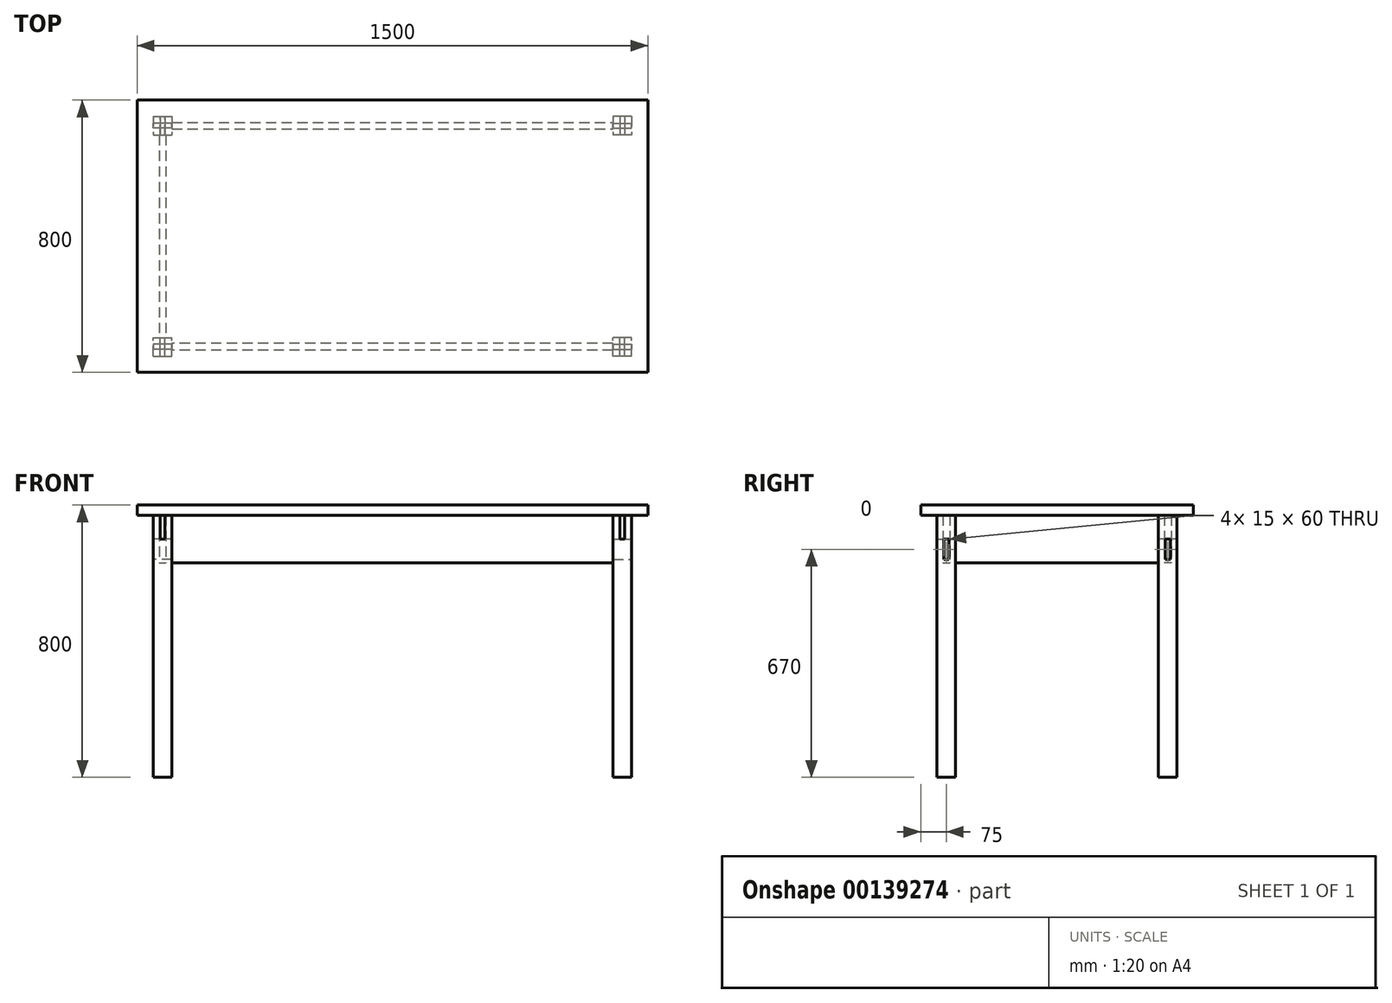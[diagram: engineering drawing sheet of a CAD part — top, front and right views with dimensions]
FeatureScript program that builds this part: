
annotation { "Feature Type Name" : "Feature", "Feature Type Description" : "" }
export const myFeature = defineFeature(function(context is Context, id is Id, definition is map)
    precondition{}
    {
        {
            assignVariable(context, id + "F0", {"name" : "oh", "anyValue" : 75});
        }
        {
            var Q0;
            Q0=qCreatedBy(makeId("Front.planeOp"),FACE);
            var sketch = newSketch(context, id + "F1", { "sketchPlane" : qUnion([Q0])});
            skLineSegment(sketch, "E0.bottom", {"start": v(-750, 800) * mm, "end": v(750, 800) * mm, "construction": true});
            skLineSegment(sketch, "E0.top", {"start": v(-750, 0) * mm, "end": v(750, 0) * mm, "construction": true});
            skLineSegment(sketch, "E0.left", {"start": v(-750, 800) * mm, "end": v(-750, 0) * mm, "construction": true});
            skLineSegment(sketch, "E0.right", {"start": v(750, 800) * mm, "end": v(750, 0) * mm, "construction": true});
            skLineSegment(sketch, "E1", {"start": v(0, 0) * mm, "end": v(0, 800) * mm, "construction": true});
            skLineSegment(sketch, "E2.bottom", {"start": v(-750, 800) * mm, "end": v(750, 800) * mm});
            skLineSegment(sketch, "E2.top", {"start": v(-750, 770) * mm, "end": v(750, 770) * mm});
            skLineSegment(sketch, "E2.left", {"start": v(-750, 800) * mm, "end": v(-750, 770) * mm});
            skLineSegment(sketch, "E2.right", {"start": v(750, 800) * mm, "end": v(750, 770) * mm});
            skLineSegment(sketch, "E3.bottom", {"start": v(-702.5, 770) * mm, "end": v(-647.5, 770) * mm});
            skLineSegment(sketch, "E3.top", {"start": v(-702.5, 0) * mm, "end": v(-647.5, 0) * mm});
            skLineSegment(sketch, "E3.left", {"start": v(-702.5, 770) * mm, "end": v(-702.5, 0) * mm});
            skLineSegment(sketch, "E3.right", {"start": v(-647.5, 770) * mm, "end": v(-647.5, 0) * mm});
            skLineSegment(sketch, "E4.bottom", {"start": v(-647.5, 770) * mm, "end": v(647.5, 770) * mm});
            skLineSegment(sketch, "E4.top", {"start": v(-647.5, 630) * mm, "end": v(647.5, 630) * mm});
            skLineSegment(sketch, "E4.left", {"start": v(-647.5, 770) * mm, "end": v(-647.5, 630) * mm});
            skLineSegment(sketch, "E4.right", {"start": v(647.5, 770) * mm, "end": v(647.5, 630) * mm});
            skLineSegment(sketch, "E5.bottom", {"start": v(-647.5, 700) * mm, "end": v(-702.5, 700) * mm});
            skLineSegment(sketch, "E5.top", {"start": v(-647.5, 640) * mm, "end": v(-702.5, 640) * mm});
            skLineSegment(sketch, "E5.left", {"start": v(-647.5, 700) * mm, "end": v(-647.5, 640) * mm});
            skLineSegment(sketch, "E5.right", {"start": v(-702.5, 700) * mm, "end": v(-702.5, 640) * mm});
            skLineSegment(sketch, "E6", {"start": v(-675, 770) * mm, "end": v(-675, 0) * mm, "construction": true});
            skLineSegment(sketch, "E7.MirrorCS", {"start": v(647.5, 640) * mm, "end": v(702.5, 640) * mm});
            skLineSegment(sketch, "E8.MirrorCS", {"start": v(702.5, 700) * mm, "end": v(702.5, 640) * mm});
            skLineSegment(sketch, "E9.MirrorCS", {"start": v(647.5, 700) * mm, "end": v(702.5, 700) * mm});
            skLineSegment(sketch, "E10.MirrorCS", {"start": v(647.5, 700) * mm, "end": v(647.5, 640) * mm});
            skSolve(sketch);
        }
        {
            var Q0;
            Q0=makeQuery(id+"F1.imprint","IMPRINT",FACE,{"disambiguationData":[TD([[makeQuery(id+"F1.imprint","IMPRINT",EDGE,{"derivedFrom":sQuery(id+"F1.wireOp",EDGE,"E2.bottom")}),-1.0]])]});
            extrude(context, id + "F2", {"entities" : qUnion([Q0]), "endBound" : BoundingType.SYMMETRIC, "depth" : 800 * mm});
        }
        {
            var Q0;
            Q0=makeQuery(id+"F2.opExtrude","CAP_FACE",FACE,{"disambiguationData":[OSD([sQuery(id+"F1.wireOp",EDGE,"E2.bottom"),sQuery(id+"F1.wireOp",EDGE,"E2.top"),sQuery(id+"F1.wireOp",EDGE,"E2.left"),sQuery(id+"F1.wireOp",EDGE,"E2.right"),sQuery(id+"F1.wireOp",EDGE,"E3.bottom"),sQuery(id+"F1.wireOp",EDGE,"E4.bottom")])],"isStart":false});
            cPlane(context, id + "F3", {"entities" : qUnion([Q0]), "cplaneType" : CPlaneType.OFFSET, "offset" : (getVariable(context, 'oh')) * mm, "oppositeDirection" : true, "width" : 150 * mm, "height" : 150 * mm});
        }
        {
            var Q0;
            Q0=qCreatedBy(id+"F3.planeOp",FACE);
            var sketch = newSketch(context, id + "F4", { "sketchPlane" : qUnion([Q0])});
            skLineSegment(sketch, "E11.0.0", {"start": v(647.5, 770) * mm, "end": v(-647.5, 770) * mm});
            skLineSegment(sketch, "E11.0.1", {"start": v(-647.5, 770) * mm, "end": v(-647.5, 700) * mm});
            skLineSegment(sketch, "E11.0.2", {"start": v(-647.5, 700) * mm, "end": v(-647.5, 640) * mm});
            skLineSegment(sketch, "E11.0.3", {"start": v(-647.5, 640) * mm, "end": v(-647.5, 630) * mm});
            skLineSegment(sketch, "E11.0.4", {"start": v(-647.5, 630) * mm, "end": v(647.5, 630) * mm});
            skLineSegment(sketch, "E11.0.5", {"start": v(647.5, 630) * mm, "end": v(647.5, 640) * mm});
            skLineSegment(sketch, "E11.0.6", {"start": v(647.5, 640) * mm, "end": v(647.5, 700) * mm});
            skLineSegment(sketch, "E11.0.7", {"start": v(647.5, 700) * mm, "end": v(647.5, 770) * mm});
            skLineSegment(sketch, "E11.1", {"start": v(702.5, 700) * mm, "end": v(702.5, 640) * mm});
            skLineSegment(sketch, "E11.2.0", {"start": v(647.5, 700) * mm, "end": v(647.5, 640) * mm});
            skLineSegment(sketch, "E11.2.1", {"start": v(647.5, 640) * mm, "end": v(702.5, 640) * mm});
            skLineSegment(sketch, "E11.2.2", {"start": v(702.5, 640) * mm, "end": v(702.5, 700) * mm});
            skLineSegment(sketch, "E11.2.3", {"start": v(702.5, 700) * mm, "end": v(647.5, 700) * mm});
            skLineSegment(sketch, "E12.0", {"start": v(-647.5, 700) * mm, "end": v(-702.5, 700) * mm});
            skLineSegment(sketch, "E12.1", {"start": v(-647.5, 640) * mm, "end": v(-702.5, 640) * mm});
            skLineSegment(sketch, "E12.2", {"start": v(-702.5, 700) * mm, "end": v(-702.5, 640) * mm});
            skSolve(sketch);
        }
        {
            var Q0;
            Q0=makeQuery(id+"F2.opExtrude","SWEPT_FACE",FACE,{"disambiguationData":[OSD([sQuery(id+"F1.wireOp",EDGE,"E2.left")])]});
            cPlane(context, id + "F5", {"entities" : qUnion([Q0]), "cplaneType" : CPlaneType.OFFSET, "offset" : (getVariable(context, 'oh')) * mm, "oppositeDirection" : true, "width" : 150 * mm, "height" : 150 * mm});
        }
        {
            var Q0;
            Q0=qCreatedBy(id+"F5.planeOp",FACE);
            var sketch = newSketch(context, id + "F6", { "sketchPlane" : qUnion([Q0])});
            skLineSegment(sketch, "E13.0", {"start": v(325, 700) * mm, "end": v(325, 640) * mm, "construction": true});
            skLineSegment(sketch, "E14.bottom", {"start": v(317.5, 700) * mm, "end": v(332.5, 700) * mm});
            skLineSegment(sketch, "E14.top", {"start": v(317.5, 640) * mm, "end": v(332.5, 640) * mm});
            skLineSegment(sketch, "E14.left", {"start": v(317.5, 700) * mm, "end": v(317.5, 640) * mm});
            skLineSegment(sketch, "E14.right", {"start": v(332.5, 700) * mm, "end": v(332.5, 640) * mm});
            skLineSegment(sketch, "E15.0", {"start": v(0, 770) * mm, "end": v(0, 0) * mm, "construction": true});
            skLineSegment(sketch, "E16.0", {"start": v(400, 770) * mm, "end": v(-400, 770) * mm, "construction": true});
            skLineSegment(sketch, "E17", {"start": v(325, 640) * mm, "end": v(325, 0) * mm, "construction": true});
            skLineSegment(sketch, "E18", {"start": v(325, 700) * mm, "end": v(325, 770) * mm, "construction": true});
            skLineSegment(sketch, "E19.bottom", {"start": v(-297.5, 770) * mm, "end": v(297.5, 770) * mm});
            skLineSegment(sketch, "E19.top", {"start": v(-297.5, 630) * mm, "end": v(297.5, 630) * mm});
            skLineSegment(sketch, "E19.left", {"start": v(-297.5, 770) * mm, "end": v(-297.5, 630) * mm});
            skLineSegment(sketch, "E19.right", {"start": v(297.5, 770) * mm, "end": v(297.5, 630) * mm});
            skLineSegment(sketch, "E20.bottom", {"start": v(297.5, 700) * mm, "end": v(352.5, 700) * mm});
            skLineSegment(sketch, "E20.top", {"start": v(297.5, 770) * mm, "end": v(352.5, 770) * mm});
            skLineSegment(sketch, "E20.left", {"start": v(297.5, 700) * mm, "end": v(297.5, 770) * mm});
            skLineSegment(sketch, "E20.right", {"start": v(352.5, 700) * mm, "end": v(352.5, 770) * mm});
            skLineSegment(sketch, "E21.bottom", {"start": v(335.91, 770) * mm, "end": v(335.7, 770) * mm});
            skLineSegment(sketch, "E21.top", {"start": v(335.91, 770) * mm, "end": v(335.7, 770) * mm});
            skLineSegment(sketch, "E21.left", {"start": v(335.91, 770) * mm, "end": v(335.91, 770) * mm});
            skLineSegment(sketch, "E21.right", {"start": v(335.7, 770) * mm, "end": v(335.7, 770) * mm});
            skLineSegment(sketch, "E22.MirrorCS", {"start": v(-352.5, 700) * mm, "end": v(-352.5, 770) * mm});
            skLineSegment(sketch, "E23.MirrorCS", {"start": v(-335.91, 770) * mm, "end": v(-335.7, 770) * mm});
            skLineSegment(sketch, "E24.MirrorCS", {"start": v(-317.5, 700) * mm, "end": v(-332.5, 700) * mm});
            skLineSegment(sketch, "E25.MirrorCS", {"start": v(-297.5, 700) * mm, "end": v(-352.5, 700) * mm});
            skLineSegment(sketch, "E26.MirrorCS", {"start": v(-297.5, 770) * mm, "end": v(-352.5, 770) * mm});
            skLineSegment(sketch, "E27.MirrorCS", {"start": v(-335.7, 770) * mm, "end": v(-335.7, 770) * mm});
            skLineSegment(sketch, "E28.MirrorCS", {"start": v(-297.5, 700) * mm, "end": v(-297.5, 770) * mm});
            skLineSegment(sketch, "E29.MirrorCS", {"start": v(-335.91, 770) * mm, "end": v(-335.91, 770) * mm});
            skLineSegment(sketch, "E30.MirrorCS", {"start": v(-325, 700) * mm, "end": v(-325, 770) * mm, "construction": true});
            skSolve(sketch);
        }
        {
            var Q0;
            Q0=makeQuery(id+"F4.imprint","IMPRINT",FACE,{"disambiguationData":[TD([[makeQuery(id+"F4.imprint","IMPRINT",EDGE,{"derivedFrom":sQuery(id+"F4.wireOp",EDGE,"E11.0.0")}),1.0]])]});
            var sketch = newSketch(context, id + "F7", { "sketchPlane" : qUnion([Q0])});
            skLineSegment(sketch, "E31.0", {"start": v(-675, 700) * mm, "end": v(-675, 770) * mm, "construction": true});
            skLineSegment(sketch, "E32.bottom", {"start": v(-682.5, 770) * mm, "end": v(-667.5, 770) * mm});
            skLineSegment(sketch, "E32.top", {"start": v(-682.5, 700) * mm, "end": v(-667.5, 700) * mm});
            skLineSegment(sketch, "E32.left", {"start": v(-682.5, 770) * mm, "end": v(-682.5, 700) * mm});
            skLineSegment(sketch, "E32.right", {"start": v(-667.5, 770) * mm, "end": v(-667.5, 700) * mm});
            skSolve(sketch);
        }
        {
            var Q0;
            Q0=makeQuery(id+"F4.imprint","IMPRINT",FACE,{"disambiguationData":[TD([[makeQuery(id+"F4.imprint","IMPRINT",EDGE,{"derivedFrom":sQuery(id+"F4.wireOp",EDGE,"E11.0.0")}),1.0]])]});
            var sketch = newSketch(context, id + "F8", { "sketchPlane" : qUnion([Q0])});
            skLineSegment(sketch, "E33.0", {"start": v(-702.5, 770) * mm, "end": v(-702.5, 0) * mm});
            skLineSegment(sketch, "E33.1", {"start": v(-647.5, 770) * mm, "end": v(-647.5, 0) * mm});
            skLineSegment(sketch, "E33.2", {"start": v(-702.5, 0) * mm, "end": v(-647.5, 0) * mm});
            skLineSegment(sketch, "E34", {"start": v(-702.5, 770) * mm, "end": v(-682.5, 770) * mm});
            skLineSegment(sketch, "E35.0", {"start": v(-682.5, 770) * mm, "end": v(-682.5, 700) * mm});
            skLineSegment(sketch, "E35.1", {"start": v(-667.5, 770) * mm, "end": v(-667.5, 700) * mm});
            skLineSegment(sketch, "E35.2", {"start": v(-682.5, 700) * mm, "end": v(-667.5, 700) * mm});
            skLineSegment(sketch, "E36.trimOffspring", {"start": v(-667.5, 770) * mm, "end": v(-647.5, 770) * mm});
            skSolve(sketch);
        }
        {
            var Q0;
            Q0=makeQuery(id+"F6.imprint","IMPRINT",FACE,{"disambiguationData":[TD([[makeQuery(id+"F6.imprint","IMPRINT",EDGE,{"derivedFrom":sQuery(id+"F6.wireOp",EDGE,"E19.bottom")}),-1.0]])]});
            var sketch = newSketch(context, id + "F9", { "sketchPlane" : qUnion([Q0])});
            skLineSegment(sketch, "E37.0", {"start": v(317.5, 640) * mm, "end": v(332.5, 640) * mm});
            skLineSegment(sketch, "E37.1", {"start": v(317.5, 700) * mm, "end": v(317.5, 640) * mm});
            skLineSegment(sketch, "E37.2", {"start": v(332.5, 700) * mm, "end": v(332.5, 640) * mm});
            skLineSegment(sketch, "E37.3", {"start": v(317.5, 700) * mm, "end": v(332.5, 700) * mm});
            skSolve(sketch);
        }
        {
            var Q0;
            Q0=makeQuery(id+"F4.imprint","IMPRINT",FACE,{"disambiguationData":[TD([[makeQuery(id+"F4.imprint","IMPRINT",EDGE,{"derivedFrom":sQuery(id+"F4.wireOp",EDGE,"E11.0.0")}),1.0]])]});
            extrude(context, id + "F10", {"entities" : qUnion([Q0]), "endBound" : BoundingType.SYMMETRIC, "depth" : 20 * mm});
        }
        {
            var Q0;
            Q0=makeQuery(id+"F4.imprint","IMPRINT",FACE,{"disambiguationData":[TD([[makeQuery(id+"F4.imprint","IMPRINT",EDGE,{"derivedFrom":sQuery(id+"F4.wireOp",EDGE,"E11.0.2")}),-1.0]])]});
            var Q1;
            Q1=makeQuery(id+"F4.imprint","IMPRINT",FACE,{"disambiguationData":[TD([[makeQuery(id+"F4.imprint","IMPRINT",EDGE,{"derivedFrom":sQuery(id+"F4.wireOp",EDGE,"E11.2.0")}),1.0]])]});
            extrude(context, id + "F11", {"entities" : qUnion([Q0, Q1]), "operationType" : NewBodyOperationType.ADD, "endBound" : BoundingType.SYMMETRIC, "depth" : 15 * mm});
        }
        {
            var Q0;
            Q0=makeQuery(id+"F9.imprint","IMPRINT",FACE,{"disambiguationData":[TD([[makeQuery(id+"F9.imprint","IMPRINT",EDGE,{"derivedFrom":makeQuery(id+"F6.imprint","IMPRINT",EDGE,{"derivedFrom":sQuery(id+"F6.wireOp",EDGE,"E19.bottom")})}),-1.0]])]});
            extrude(context, id + "F12", {"entities" : qUnion([Q0]), "endBound" : BoundingType.SYMMETRIC, "depth" : 20 * mm});
        }
        {
            var Q0;
            {var subQ0=sQuery(id+"F6.wireOp",EDGE,"E22.MirrorCS");Q0=makeQuery(id+"F6.imprint","IMPRINT",FACE,{"disambiguationData":[TD([[makeQuery(id+"F6.imprint","IMPRINT",EDGE,{"derivedFrom":subQ0}),-1.0]])]});}
            var Q1;
            {var subQ3=sQuery(id+"F6.wireOp",EDGE,"E20.left");Q1=makeQuery(id+"F6.imprint","IMPRINT",FACE,{"disambiguationData":[TD([[makeQuery(id+"F6.imprint","IMPRINT",EDGE,{"derivedFrom":subQ3}),-1.0]])]});}
            extrude(context, id + "F13", {"entities" : qUnion([Q0, Q1]), "operationType" : NewBodyOperationType.ADD, "endBound" : BoundingType.SYMMETRIC, "depth" : 15 * mm});
        }
        {
            var Q0;
            Q0=makeQuery(id+"F8.imprint","IMPRINT",FACE,{"disambiguationData":[TD([[makeQuery(id+"F8.imprint","IMPRINT",EDGE,{"derivedFrom":sQuery(id+"F8.wireOp",EDGE,"E33.0")}),1.0]])]});
            extrude(context, id + "F14", {"entities" : qUnion([Q0]), "endBound" : BoundingType.SYMMETRIC, "depth" : 55 * mm});
        }
        {
            var Q0;
            Q0=makeQuery(id+"F9.imprint","IMPRINT",FACE,{"disambiguationData":[TD([[makeQuery(id+"F9.imprint","IMPRINT",EDGE,{"derivedFrom":sQuery(id+"F9.wireOp",EDGE,"E37.0")}),1.0]])]});
            extrude(context, id + "F15", {"entities" : qUnion([Q0]), "operationType" : NewBodyOperationType.REMOVE, "endBound" : BoundingType.SYMMETRIC, "oppositeDirection" : true, "depth" : 55 * mm});
        }
        {
            var Q0;
            Q0=makeQuery(id+"F10.opExtrude","SWEPT_BODY",BODY,{"disambiguationData":[OSD([sQuery(id+"F4.wireOp",EDGE,"E11.0.0"),sQuery(id+"F4.wireOp",EDGE,"E11.0.1"),sQuery(id+"F4.wireOp",EDGE,"E11.0.2"),sQuery(id+"F4.wireOp",EDGE,"E11.0.3"),sQuery(id+"F4.wireOp",EDGE,"E11.0.4"),sQuery(id+"F4.wireOp",EDGE,"E11.0.5"),sQuery(id+"F4.wireOp",EDGE,"E11.0.7"),sQuery(id+"F4.wireOp",EDGE,"E11.2.0")])]});
            var Q1;
            Q1=makeQuery(id+"F14.opExtrude","SWEPT_BODY",BODY,{"disambiguationData":[OSD([sQuery(id+"F8.wireOp",EDGE,"E33.0"),sQuery(id+"F8.wireOp",EDGE,"E33.1"),sQuery(id+"F8.wireOp",EDGE,"E33.2"),sQuery(id+"F8.wireOp",EDGE,"E34"),sQuery(id+"F8.wireOp",EDGE,"E35.0"),sQuery(id+"F8.wireOp",EDGE,"E35.1"),sQuery(id+"F8.wireOp",EDGE,"E35.2"),sQuery(id+"F8.wireOp",EDGE,"E36.trimOffspring")])]});
            var Q2;
            Q2=sQuery(id+"F1.wireOp",EDGE,"E1");
            circularPattern(context, id + "F16", {"entities" : qUnion([Q0, Q1]), "axis" : qUnion([Q2]), "angle" : 180 * degree, "instanceCount" : 2});
        }
        {
            var Q0;
            Q0=makeQuery(id+"F14.opExtrude","SWEPT_BODY",BODY,{"disambiguationData":[OSD([sQuery(id+"F8.wireOp",EDGE,"E33.0"),sQuery(id+"F8.wireOp",EDGE,"E33.1"),sQuery(id+"F8.wireOp",EDGE,"E33.2"),sQuery(id+"F8.wireOp",EDGE,"E34"),sQuery(id+"F8.wireOp",EDGE,"E35.0"),sQuery(id+"F8.wireOp",EDGE,"E35.1"),sQuery(id+"F8.wireOp",EDGE,"E35.2"),sQuery(id+"F8.wireOp",EDGE,"E36.trimOffspring")])]});
            var Q1;
            Q1=qCreatedBy(makeId("Front.planeOp"),FACE);
            mirror(context, id + "F17", {"entities" : qUnion([Q0]), "mirrorPlane" : qUnion([Q1])});
        }
        {
            var Q0;
            Q0=makeQuery(id+"F12.opExtrude","SWEPT_BODY",BODY,{"disambiguationData":[OSD([sQuery(id+"F6.wireOp",EDGE,"E19.bottom"),sQuery(id+"F6.wireOp",EDGE,"E19.top"),sQuery(id+"F6.wireOp",EDGE,"E19.left"),sQuery(id+"F6.wireOp",EDGE,"E19.right"),sQuery(id+"F6.wireOp",EDGE,"E20.left"),sQuery(id+"F6.wireOp",EDGE,"E28.MirrorCS")])]});
            var Q1;
            Q1=makeQuery(id+"F14.opExtrude","SWEPT_BODY",BODY,{"disambiguationData":[OSD([sQuery(id+"F8.wireOp",EDGE,"E33.0"),sQuery(id+"F8.wireOp",EDGE,"E33.1"),sQuery(id+"F8.wireOp",EDGE,"E33.2"),sQuery(id+"F8.wireOp",EDGE,"E34"),sQuery(id+"F8.wireOp",EDGE,"E35.0"),sQuery(id+"F8.wireOp",EDGE,"E35.1"),sQuery(id+"F8.wireOp",EDGE,"E35.2"),sQuery(id+"F8.wireOp",EDGE,"E36.trimOffspring")])]});
            var Q2;
            Q2=qCreatedBy(makeId("Right.planeOp"),FACE);
            mirror(context, id + "F18", {"entities" : qUnion([Q0, Q1]), "mirrorPlane" : qUnion([Q2])});
        }
    });
